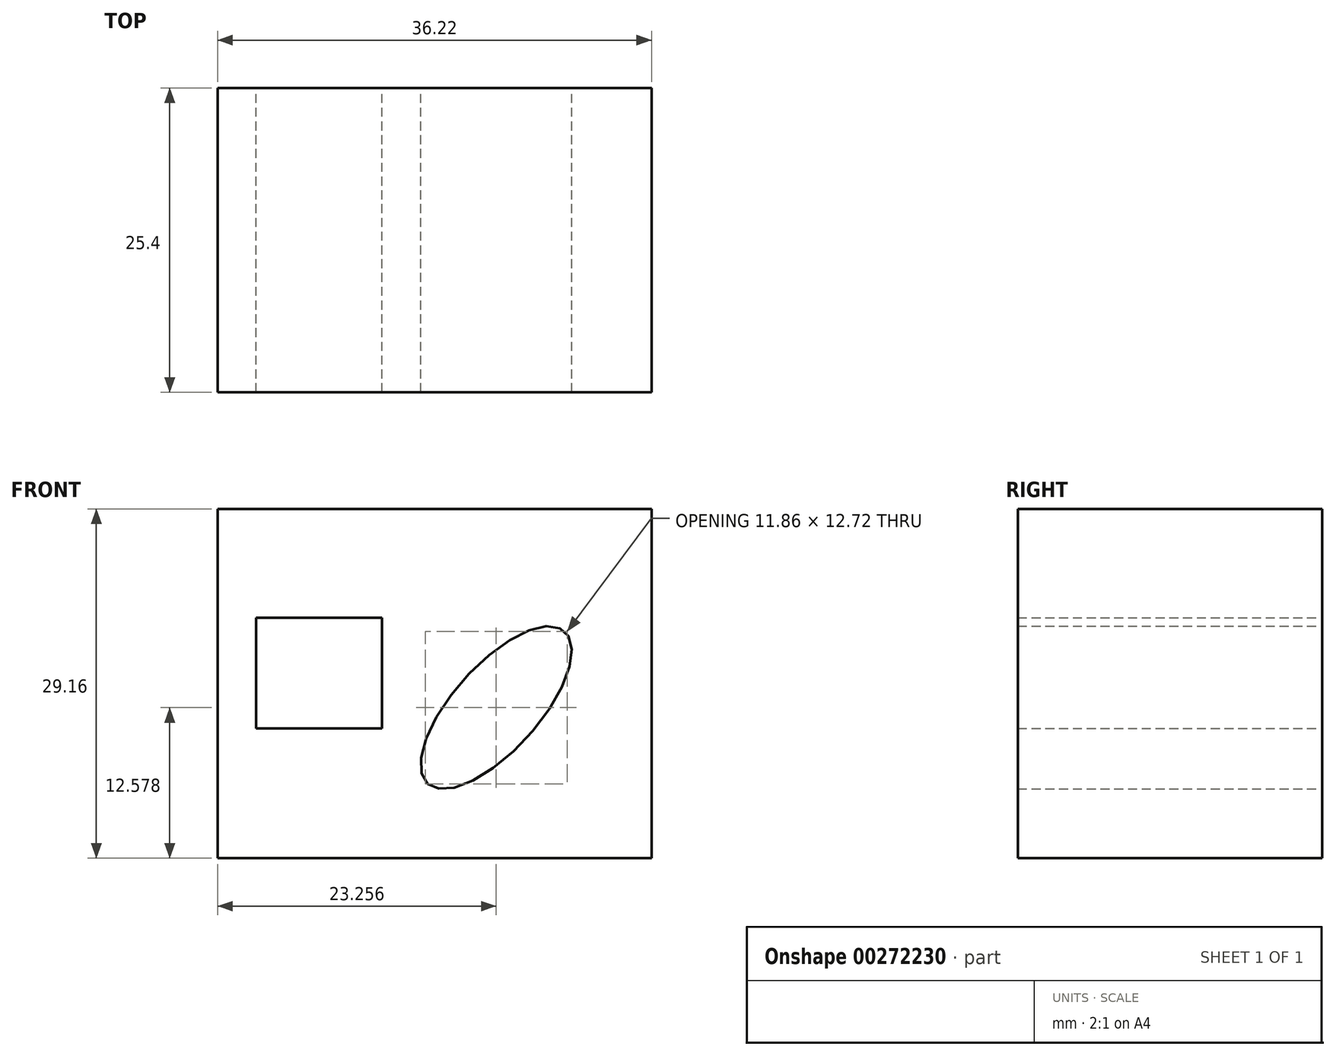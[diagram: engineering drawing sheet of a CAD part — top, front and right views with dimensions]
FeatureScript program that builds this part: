
annotation { "Feature Type Name" : "Feature", "Feature Type Description" : "" }
export const myFeature = defineFeature(function(context is Context, id is Id, definition is map)
    precondition{}
    {
        {
            var Q0;
            Q0=qCreatedBy(makeId("Front.planeOp"),FACE);
            var sketch = newSketch(context, id + "F0", { "sketchPlane" : qUnion([Q0])});
            skLineSegment(sketch, "E0.bottom", {"start": v(-60.89, 61.83) * mm, "end": v(-50.4, 61.83) * mm});
            skLineSegment(sketch, "E0.top", {"start": v(-60.89, 52.59) * mm, "end": v(-50.4, 52.59) * mm});
            skLineSegment(sketch, "E0.left", {"start": v(-60.89, 61.83) * mm, "end": v(-60.89, 52.59) * mm});
            skLineSegment(sketch, "E0.right", {"start": v(-50.4, 61.83) * mm, "end": v(-50.4, 52.59) * mm});
            skEllipse(sketch, "E1", {"center": v(-40.85, 54.32) * mm, "majorRadius": 8.56 * mm, "minorRadius": 3.58 * mm, "majorAxis": v(-0.67, -0.74)});
            skLineSegment(sketch, "E2.bottom", {"start": v(-64.1, 70.9) * mm, "end": v(-27.9, 70.9) * mm});
            skLineSegment(sketch, "E2.top", {"start": v(-64.1, 41.74) * mm, "end": v(-27.9, 41.74) * mm});
            skLineSegment(sketch, "E2.left", {"start": v(-64.1, 70.9) * mm, "end": v(-64.1, 41.74) * mm});
            skLineSegment(sketch, "E2.right", {"start": v(-27.9, 70.9) * mm, "end": v(-27.9, 41.74) * mm});
            skSolve(sketch);
        }
        {
            var Q0;
            Q0 = qSketchRegion(id + "F0", true);
            extrude(context, id + "F1", {"entities" : qUnion([Q0]), "depth" : 25.4 * mm});
        }
    });
